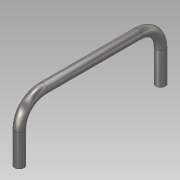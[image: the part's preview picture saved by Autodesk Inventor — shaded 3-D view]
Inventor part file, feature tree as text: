
AUTODESK INVENTOR PART (.ipt)
format: ipt  version: 2019 (Build 230136000, 136)  size: 102,912 bytes
history: native  units: mm
features: sketch x2, other x1, sweep x1
ambient origin geometry x8: Origin, YZ Plane, XZ Plane, XY Plane, X Axis, Y Axis, Z Axis, Center Point
bodies: Body1 (feature_tree)
feature tree (4):
  other  "Sólido1"
  sweep  "Barrido1"
  sketch  "Boceto1"  dims[d0=35.0mm d1=90.0mm]
  sketch  "Boceto2"  dims[d2=15.0mm d3=6.0mm d4=0.0mm d5=0.0mm]
